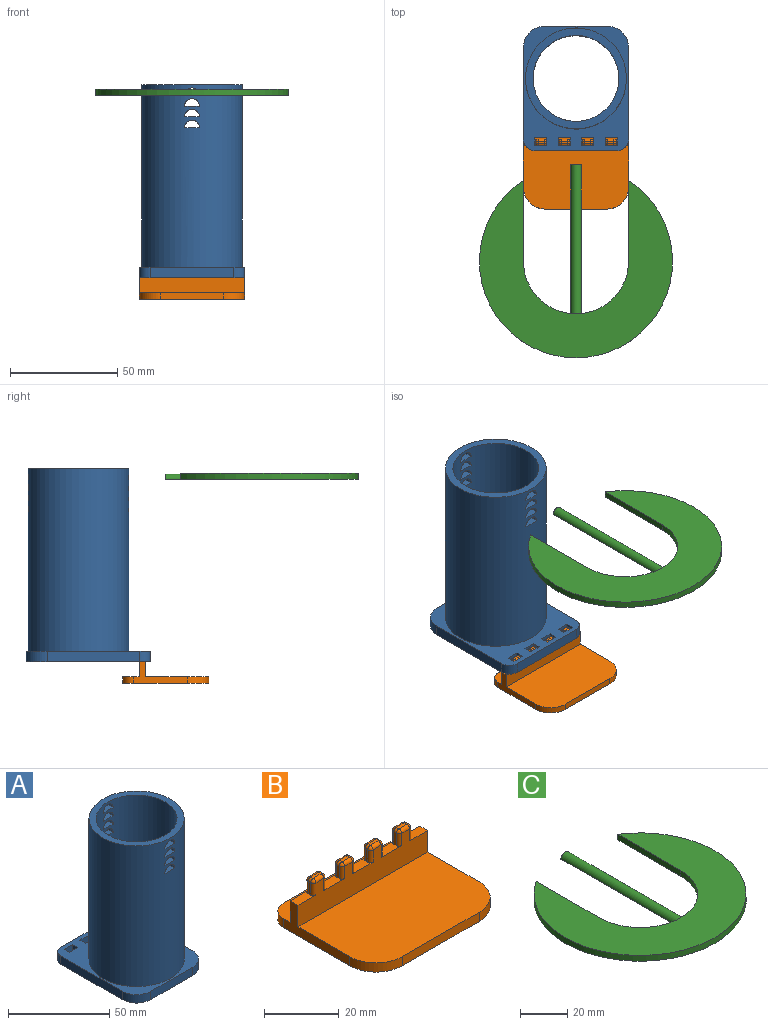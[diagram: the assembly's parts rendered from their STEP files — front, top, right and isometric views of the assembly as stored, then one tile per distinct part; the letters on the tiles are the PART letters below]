
ASSEMBLY  parts=3 mates=4
PART A: 45 faces, bbox 49x58x90 mm
  f0: plane 43x5mm, normal (-1,0,0), area 215mm2, adj f21,f22,f26,f27
  f1: plane 29x5mm, normal (0,-1,0), area 145mm2, adj f21,f22,f27,f28
  f2: plane 43x5mm, normal (1,0,0), area 215mm2, adj f21,f22,f25,f28
  f3: plane 5x3.7mm, normal (1,0,0), area 18.5mm2, adj f4,f16,f21,f22
  f4: plane 5.7x5mm, normal (0,-1,0), area 28.5mm2, adj f3,f5,f21,f22
  f5: plane 5x3.7mm, normal (-1,0,0), area 18.5mm2, adj f4,f16,f21,f22
  f6: plane 5x3.7mm, normal (1,0,0), area 18.5mm2, adj f7,f17,f21,f22
  f7: plane 5.7x5mm, normal (0,-1,0), area 28.5mm2, adj f6,f8,f21,f22
  f8: plane 5x3.7mm, normal (-1,0,0), area 18.5mm2, adj f7,f17,f21,f22
  f9: plane 5x3.7mm, normal (1,0,0), area 18.5mm2, adj f10,f18,f21,f22
  f10: plane 5.7x5mm, normal (0,-1,0), area 28.5mm2, adj f9,f11,f21,f22
  f11: plane 5x3.7mm, normal (-1,0,0), area 18.5mm2, adj f10,f18,f21,f22
  f12: plane 5x3.7mm, normal (1,0,0), area 18.5mm2, adj f13,f19,f21,f22
  f13: plane 5.7x5mm, normal (0,-1,0), area 28.5mm2, adj f12,f14,f21,f22
  f14: plane 5x3.7mm, normal (-1,0,0), area 18.5mm2, adj f13,f19,f21,f22
  f15: plane 39x5mm, normal (0,1,0), area 195mm2, adj f21,f22,f25,f26
  f16: plane 5.7x5mm, normal (0,1,0), area 28.5mm2, adj f3,f5,f21,f22
  f17: plane 5.7x5mm, normal (0,1,0), area 28.5mm2, adj f6,f8,f21,f22
  f18: plane 5.7x5mm, normal (0,1,0), area 28.5mm2, adj f9,f11,f21,f22
  f19: plane 5.7x5mm, normal (0,1,0), area 28.5mm2, adj f12,f14,f21,f22
  f20: cylinder r=20mm len=90mm, axis (0,0,-1), area 11155.1mm2, adj f22,f24,f29,f30,f31,f32,f33,f34
  f21: plane 58x49mm, normal (0,0,1), area 969mm2, adj f0,f1,f2,f3,f4,f5,f6,f7
  f22: plane 58x49mm, normal (0,0,-1), area 1447.4mm2, adj f0,f1,f2,f3,f4,f5,f6,f7
  f23: cylinder r=23.5mm len=85mm, axis (0,0,-1), area 12396.1mm2, adj f21,f24,f29,f30,f31,f32,f33,f34
  f24: plane 47x47mm, normal (0,0,1), area 478.3mm2, adj f20,f23
  f25: cylinder r=5mm len=5mm, axis (0,0,-1), area 39.3mm2, adj f2,f15,f21,f22
  f26: cylinder r=5mm len=5mm, axis (0,0,1), area 39.3mm2, adj f0,f15,f21,f22
  f27: cylinder r=10mm len=10mm, axis (0,0,-1), area 78.5mm2, adj f0,f1,f21,f22
  f28: cylinder r=10mm len=10mm, axis (0,0,1), area 78.5mm2, adj f1,f2,f21,f22
  f29: plane 7x3.81mm, normal (0,0,1), area 24.6mm2, adj f20,f23,f30
  f30: cylinder r=3.5mm len=7mm, axis (0,-1,0), area 38.7mm2, adj f20,f23,f29
  f31: cylinder r=3.5mm len=7mm, axis (0,-1,0), area 38.7mm2, adj f20,f23,f32
  f32: plane 7x3.81mm, normal (0,0,1), area 24.6mm2, adj f20,f23,f31
  f33: plane 7x3.81mm, normal (0,0,1), area 24.6mm2, adj f20,f23,f34
  f34: cylinder r=3.5mm len=7mm, axis (0,-1,0), area 38.7mm2, adj f20,f23,f33
  f35: cylinder r=3.5mm len=7mm, axis (0,-1,0), area 38.7mm2, adj f20,f23,f36
  f36: plane 7x3.81mm, normal (0,0,1), area 24.6mm2, adj f20,f23,f35
  f37: plane 7x3.81mm, normal (0,0,1), area 24.6mm2, adj f20,f23,f38
  f38: cylinder r=3.5mm len=7mm, axis (0,-1,0), area 38.7mm2, adj f20,f23,f37
  f39: cylinder r=3.5mm len=7mm, axis (0,-1,0), area 38.7mm2, adj f20,f23,f40
  f40: plane 7x3.81mm, normal (0,0,1), area 24.6mm2, adj f20,f23,f39
  f41: plane 7x3.81mm, normal (0,0,1), area 24.6mm2, adj f20,f23,f42
  f42: cylinder r=3.5mm len=7mm, axis (0,-1,0), area 38.7mm2, adj f20,f23,f41
  f43: cylinder r=3.5mm len=7mm, axis (0,-1,0), area 38.7mm2, adj f20,f23,f44
  f44: plane 7x3.81mm, normal (0,0,1), area 24.6mm2, adj f20,f23,f43
PART B: 78 faces, bbox 49x40x15 mm
  f0: plane 49x7.5mm, normal (0,0,1), area 356.8mm2, adj f2,f3,f5,f7,f74,f75
  f1: plane 49x29.5mm, normal (0,0,1), area 1402.6mm2, adj f3,f4,f5,f9,f76,f77
  f2: plane 39x3mm, normal (0,1,0), area 117mm2, adj f0,f6,f74,f75
  f3: plane 25x10mm, normal (-1,0,0), area 96mm2, adj f0,f1,f6,f7,f9,f21,f75,f76
  f4: plane 29x3mm, normal (0,-1,0), area 87mm2, adj f1,f6,f76,f77
  f5: plane 25x10mm, normal (1,0,0), area 96mm2, adj f0,f1,f6,f7,f9,f22,f74,f77
  f6: plane 49x40mm, normal (0,0,-1), area 1906.3mm2, adj f2,f3,f4,f5,f74,f75,f76,f77
  f7: plane 49x11mm, normal (0,1,0), area 391mm2, adj f0,f3,f5,f21,f22,f23,f24,f25
  f8: plane 4x1mm, normal (-1,0,0), area 4mm2, adj f21,f62,f66,f67
  f9: plane 49x11mm, normal (0,-1,0), area 391mm2, adj f1,f3,f5,f21,f22,f23,f24,f25
  f10: plane 4x1mm, normal (1,0,0), area 4mm2, adj f23,f64,f70,f73
  f11: plane 3x1mm, normal (0,0,1), area 3mm2, adj f65,f66,f70,f71
  f12: plane 4x1mm, normal (-1,0,0), area 4mm2, adj f23,f52,f58,f61
  f13: plane 4x1mm, normal (1,0,0), area 4mm2, adj f24,f50,f54,f55
  f14: plane 3x1mm, normal (0,0,1), area 3mm2, adj f53,f54,f58,f59
  f15: plane 4x1mm, normal (-1,0,0), area 4mm2, adj f24,f38,f42,f43
  f16: plane 4x1mm, normal (1,0,0), area 4mm2, adj f25,f40,f46,f49
  f17: plane 3x1mm, normal (0,0,1), area 3mm2, adj f41,f42,f46,f47
  f18: plane 4x1mm, normal (-1,0,0), area 4mm2, adj f25,f31,f35,f37
  f19: plane 4x1mm, normal (1,0,0), area 4mm2, adj f22,f26,f28,f29
  f20: plane 3x1mm, normal (0,0,1), area 3mm2, adj f29,f30,f34,f35
  f21: plane 6.8x3mm, normal (0,0,1), area 17.8mm2, adj f3,f7,f8,f9,f62,f67
  f22: plane 6.8x3mm, normal (0,0,1), area 17.8mm2, adj f5,f7,f9,f19,f26,f28
  f23: plane 7.8x3mm, normal (0,0,1), area 18.3mm2, adj f7,f9,f10,f12,f52,f61,f64,f73
  f24: plane 7.8x3mm, normal (0,0,1), area 18.3mm2, adj f7,f9,f13,f15,f38,f43,f50,f55
  f25: plane 7.8x3mm, normal (0,0,1), area 18.3mm2, adj f7,f9,f16,f18,f31,f37,f40,f49
  f26: cylinder r=1mm len=4mm, axis (0,0,1), area 6.3mm2, adj f9,f19,f22,f27
  f27: sphere r=1mm, area 1.6mm2, adj f26,f29,f30
  f28: cylinder r=1mm len=4mm, axis (0,0,-1), area 6.3mm2, adj f7,f19,f22,f32
  f29: cylinder r=1mm len=1mm, axis (0,-1,0), area 1.6mm2, adj f19,f20,f27,f32
  f30: cylinder r=1mm len=3mm, axis (-1,0,0), area 4.7mm2, adj f9,f20,f27,f33
  f31: cylinder r=1mm len=4mm, axis (0,0,-1), area 6.3mm2, adj f9,f18,f25,f33
  f32: sphere r=1mm, area 1.6mm2, adj f28,f29,f34
  f33: sphere r=1mm, area 1.6mm2, adj f30,f31,f35
  f34: cylinder r=1mm len=3mm, axis (1,0,0), area 4.7mm2, adj f7,f20,f32,f36
  f35: cylinder r=1mm len=1mm, axis (0,1,0), area 1.6mm2, adj f18,f20,f33,f36
  f36: sphere r=1mm, area 1.6mm2, adj f34,f35,f37
  f37: cylinder r=1mm len=4mm, axis (0,0,1), area 6.3mm2, adj f7,f18,f25,f36
  f38: cylinder r=1mm len=4mm, axis (0,0,-1), area 6.3mm2, adj f9,f15,f24,f39
  f39: sphere r=1mm, area 1.6mm2, adj f38,f41,f42
  f40: cylinder r=1mm len=4mm, axis (0,0,1), area 6.3mm2, adj f9,f16,f25,f44
  f41: cylinder r=1mm len=3mm, axis (-1,0,0), area 4.7mm2, adj f9,f17,f39,f44
  f42: cylinder r=1mm len=1mm, axis (0,1,0), area 1.6mm2, adj f15,f17,f39,f45
  f43: cylinder r=1mm len=4mm, axis (0,0,1), area 6.3mm2, adj f7,f15,f24,f45
  f44: sphere r=1mm, area 1.6mm2, adj f40,f41,f46
  f45: sphere r=1mm, area 1.6mm2, adj f42,f43,f47
  f46: cylinder r=1mm len=1mm, axis (0,-1,0), area 1.6mm2, adj f16,f17,f44,f48
  f47: cylinder r=1mm len=3mm, axis (1,0,0), area 4.7mm2, adj f7,f17,f45,f48
  f48: sphere r=1mm, area 1.6mm2, adj f46,f47,f49
  f49: cylinder r=1mm len=4mm, axis (0,0,-1), area 6.3mm2, adj f7,f16,f25,f48
  f50: cylinder r=1mm len=4mm, axis (0,0,-1), area 6.3mm2, adj f7,f13,f24,f51
  f51: sphere r=1mm, area 1.6mm2, adj f50,f53,f54
  f52: cylinder r=1mm len=4mm, axis (0,0,1), area 6.3mm2, adj f7,f12,f23,f56
  f53: cylinder r=1mm len=3mm, axis (1,0,0), area 4.7mm2, adj f7,f14,f51,f56
  f54: cylinder r=1mm len=1mm, axis (0,-1,0), area 1.6mm2, adj f13,f14,f51,f57
  f55: cylinder r=1mm len=4mm, axis (0,0,1), area 6.3mm2, adj f9,f13,f24,f57
  f56: sphere r=1mm, area 1.6mm2, adj f52,f53,f58
  f57: sphere r=1mm, area 1.6mm2, adj f54,f55,f59
  f58: cylinder r=1mm len=1mm, axis (0,1,0), area 1.6mm2, adj f12,f14,f56,f60
  f59: cylinder r=1mm len=3mm, axis (-1,0,0), area 4.7mm2, adj f9,f14,f57,f60
  f60: sphere r=1mm, area 1.6mm2, adj f58,f59,f61
  f61: cylinder r=1mm len=4mm, axis (0,0,-1), area 6.3mm2, adj f9,f12,f23,f60
  f62: cylinder r=1mm len=4mm, axis (0,0,-1), area 6.3mm2, adj f8,f9,f21,f63
  f63: sphere r=1mm, area 1.6mm2, adj f62,f65,f66
  f64: cylinder r=1mm len=4mm, axis (0,0,1), area 6.3mm2, adj f9,f10,f23,f68
  f65: cylinder r=1mm len=3mm, axis (-1,0,0), area 4.7mm2, adj f9,f11,f63,f68
  f66: cylinder r=1mm len=1mm, axis (0,1,0), area 1.6mm2, adj f8,f11,f63,f69
  f67: cylinder r=1mm len=4mm, axis (0,0,1), area 6.3mm2, adj f7,f8,f21,f69
  f68: sphere r=1mm, area 1.6mm2, adj f64,f65,f70
  f69: sphere r=1mm, area 1.6mm2, adj f66,f67,f71
  f70: cylinder r=1mm len=1mm, axis (0,-1,0), area 1.6mm2, adj f10,f11,f68,f72
  f71: cylinder r=1mm len=3mm, axis (1,0,0), area 4.7mm2, adj f7,f11,f69,f72
  f72: sphere r=1mm, area 1.6mm2, adj f70,f71,f73
  f73: cylinder r=1mm len=4mm, axis (0,0,-1), area 6.3mm2, adj f7,f10,f23,f72
  f74: cylinder r=5mm len=5mm, axis (0,0,1), area 23.6mm2, adj f0,f2,f5,f6
  f75: cylinder r=5mm len=5mm, axis (0,0,-1), area 23.6mm2, adj f0,f2,f3,f6
  f76: cylinder r=10mm len=10mm, axis (0,0,1), area 47.1mm2, adj f1,f3,f4,f6
  f77: cylinder r=10mm len=10mm, axis (0,0,-1), area 47.1mm2, adj f1,f4,f5,f6
PART C: 10 faces, bbox 90x89.9x3 mm
  f0: plane 5x2.5mm, normal (0,1,0), area 9.8mm2, adj f7,f9
  f1: plane 37.75x3mm, normal (1,0,0), area 113.2mm2, adj f2,f5,f6,f7
  f2: cylinder r=45mm len=90mm, axis (0,0,-1), area 692.8mm2, adj f1,f3,f6,f7
  f3: plane 37.75x3mm, normal (-1,0,0), area 113.2mm2, adj f2,f4,f6,f7
  f4: cylinder r=24.5mm len=24.37mm, axis (0,0,-1), area 107.9mm2, adj f3,f6,f7,f8
  f5: cylinder r=24.5mm len=24.37mm, axis (0,0,-1), area 107.9mm2, adj f1,f6,f7,f8
  f6: plane 90x82.75mm, normal (0,0,1), area 3328.7mm2, adj f1,f2,f3,f4,f5,f8
  f7: plane 90x89.93mm, normal (0,0,-1), area 3675.2mm2, adj f0,f1,f2,f3,f4,f5,f9
  f8: plane 5x3mm, normal (0,1,0), area 5.2mm2, adj f4,f5,f6,f9
  f9: cylinder r=2.5mm len=69.3mm, axis (0,1,0), area 544.3mm2, adj f0,f7,f8
PLACE A rot(axis=(0,0,1),180deg) t=(24.5,145.2,10)mm
PLACE B rot(axis=(0,0,1),0deg) t=(-24.5,0,0)mm
PLACE C rot(axis=(0,0,1),0deg) t=(102.5,-88.6,95)mm
MATE planar C.f7 <-> A.f41  axis (0,0,-1) through (0,20.4,95)mm
MATE cylindrical A.f42 <-> C.f9  axis (0,1,0) through (0,39.1,95)mm
MATE planar B.f3 <-> A.f2  axis (-1,0,0) through (-24.5,31,10)mm
MATE planar B.f9 <-> A.f4  axis (0,-1,0) through (17.7,29.5,10)mm
